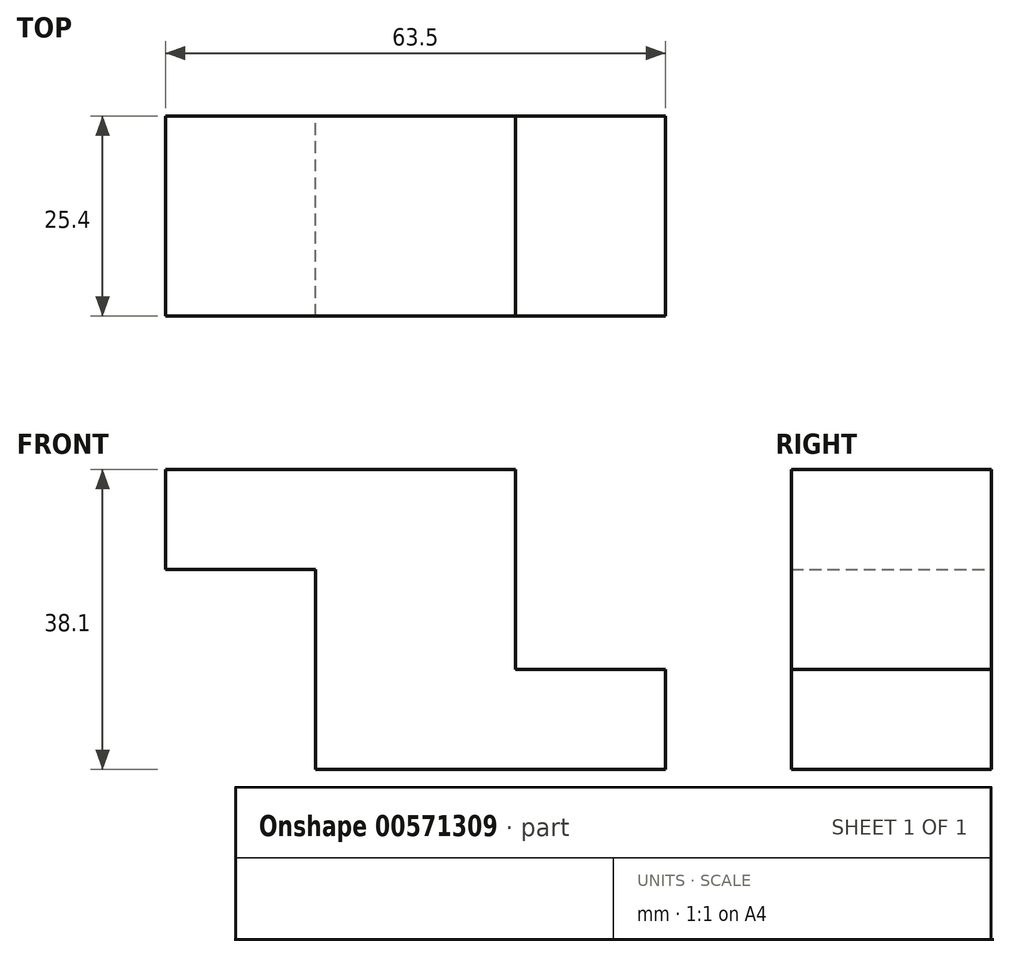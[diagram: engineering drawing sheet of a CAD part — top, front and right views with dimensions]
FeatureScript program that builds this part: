
annotation { "Feature Type Name" : "Feature", "Feature Type Description" : "" }
export const myFeature = defineFeature(function(context is Context, id is Id, definition is map)
    precondition{}
    {
        {
            var Q0;
            Q0=qCreatedBy(makeId("Front.planeOp"),FACE);
            var sketch = newSketch(context, id + "F0", { "sketchPlane" : qUnion([Q0])});
            skLineSegment(sketch, "E0.bottom", {"start": v(0, 38.1) * mm, "end": v(44.45, 38.1) * mm});
            skLineSegment(sketch, "E0.top", {"start": v(19.05, 0) * mm, "end": v(63.5, 0) * mm});
            skLineSegment(sketch, "E0.left", {"start": v(0, 38.1) * mm, "end": v(0, 25.4) * mm});
            skLineSegment(sketch, "E0.right", {"start": v(63.5, 12.7) * mm, "end": v(63.5, 0) * mm});
            skLineSegment(sketch, "E1", {"start": v(0, 25.4) * mm, "end": v(19.05, 25.4) * mm});
            skLineSegment(sketch, "E2", {"start": v(19.05, 25.4) * mm, "end": v(19.05, 0) * mm});
            skLineSegment(sketch, "E3", {"start": v(63.5, 12.7) * mm, "end": v(44.45, 12.7) * mm});
            skLineSegment(sketch, "E4", {"start": v(44.45, 12.7) * mm, "end": v(44.45, 38.1) * mm});
            skSolve(sketch);
        }
        {
            var Q0;
            Q0 = qSketchRegion(id + "F0", true);
            extrude(context, id + "F1", {"entities" : qUnion([Q0]), "depth" : 25.4 * mm, "offsetDistance" : 25.4 * mm});
        }
    });
